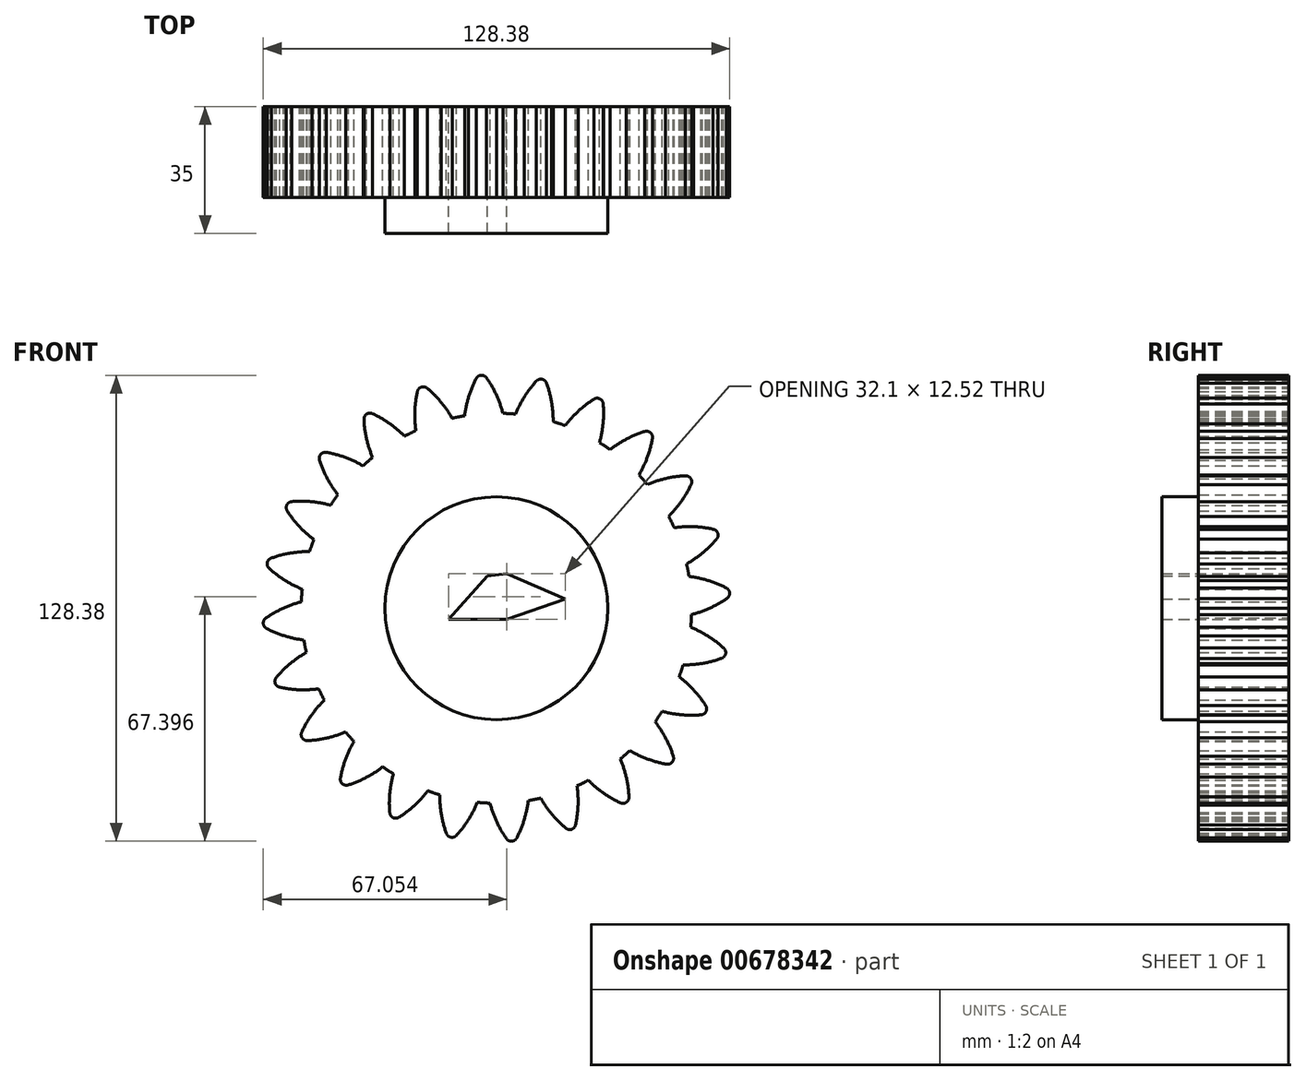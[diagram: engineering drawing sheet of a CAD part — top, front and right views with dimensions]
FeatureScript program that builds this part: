
annotation { "Feature Type Name" : "Feature", "Feature Type Description" : "" }
export const myFeature = defineFeature(function(context is Context, id is Id, definition is map)
    precondition{}
    {
        {
            var Q0;
            Q0=qCreatedBy(makeId("Front.planeOp"),FACE);
            var sketch = newSketch(context, id + "F0", { "sketchPlane" : qUnion([Q0])});
            skCircle(sketch, "E0", {"center": v(0, 0) * mm, "radius": 53.72 * mm});
            skCircle(sketch, "E1", {"center": v(0, 0) * mm, "radius": 58.67 * mm, "construction": true});
            skCircle(sketch, "E2", {"center": v(0, 0) * mm, "radius": 63.5 * mm, "construction": true});
            skLineSegment(sketch, "E3", {"start": v(0, 0) * mm, "end": v(0, 77.82) * mm, "construction": true});
            skLineSegment(sketch, "E4", {"start": v(0, 0) * mm, "end": v(-5.67, 86.58) * mm, "construction": true});
            skLineSegment(sketch, "E5", {"start": v(0, 58.67) * mm, "end": v(-52.15, 58.67) * mm, "construction": true});
            skLineSegment(sketch, "E6", {"start": v(-52.15, 58.67) * mm, "end": v(-65.26, 58.67) * mm, "construction": true});
            skLineSegment(sketch, "E7", {"start": v(0, 58.67) * mm, "end": v(-71.37, 38.87) * mm, "construction": true});
            skLineSegment(sketch, "E8", {"start": v(-55.2, 58.67) * mm, "end": v(-61.48, 58.67) * mm, "construction": true});
            skCircle(sketch, "E9", {"center": v(0, 0) * mm, "radius": 56.54 * mm, "construction": true});
            skCircle(sketch, "E10", {"center": v(0, 58.67) * mm, "radius": 30.43 * mm, "construction": true});
            skCircle(sketch, "E11", {"center": v(-27.68, 46.04) * mm, "radius": 30.43 * mm, "construction": true});
            skArc(sketch, "E12", {"start": v(0, 58.67) * mm, "mid": v(-1.24, 61.13) * mm, "end": v(-2.72, 63.44) * mm});
            skArc(sketch, "E13", {"start": v(1.77, 53.7) * mm, "mid": v(1, 56.22) * mm, "end": v(0, 58.67) * mm});
            skArc(sketch, "E14.MirrorCS", {"start": v(-7.66, 58.17) * mm, "mid": v(-6.75, 60.76) * mm, "end": v(-5.58, 63.25) * mm});
            skArc(sketch, "E15.MirrorCS", {"start": v(-8.76, 53) * mm, "mid": v(-8.33, 55.61) * mm, "end": v(-7.66, 58.17) * mm});
            skArc(sketch, "E16", {"start": v(-2.72, 63.44) * mm, "mid": v(-4.2, 64.18) * mm, "end": v(-5.58, 63.25) * mm});
            skCircle(sketch, "E17", {"center": v(0, 0) * mm, "radius": 30.7 * mm});
            skLineSegment(sketch, "E18", {"start": v(2.8, 9.47) * mm, "end": v(18.91, 2.54) * mm});
            skLineSegment(sketch, "E19", {"start": v(18.91, 2.54) * mm, "end": v(2.8, -3.06) * mm});
            skLineSegment(sketch, "E20", {"start": v(2.8, -3.06) * mm, "end": v(-13.18, -3.06) * mm});
            skLineSegment(sketch, "E21", {"start": v(-13.18, -3.06) * mm, "end": v(-2.45, 8.9) * mm});
            skLineSegment(sketch, "E22", {"start": v(-2.45, 8.9) * mm, "end": v(2.8, 9.47) * mm});
            skSolve(sketch);
        }
        {
            var Q0;
            {var subQ0=sQuery(id+"F0.wireOp",EDGE,"E0");var subQ1=makeQuery(id+"F0.imprint","INTERSECT",VERTEX,{"derivedFrom":[subQ0,sQuery(id+"F0.wireOp",EDGE,"E13")]});Q0=makeQuery(id+"F0.imprint","IMPRINT",FACE,{"disambiguationData":[TD([[makeQuery(id+"F0.imprint","IMPRINT",EDGE,{"disambiguationData":[TD([[subQ1,-1.0]])],"derivedFrom":subQ0}),1.0]])]});}
            var Q1;
            Q1=makeQuery(id+"F0.imprint","IMPRINT",FACE,{"disambiguationData":[TD([[makeQuery(id+"F0.imprint","IMPRINT",EDGE,{"derivedFrom":sQuery(id+"F0.wireOp",EDGE,"E12")}),1.0]])]});
            extrude(context, id + "F1", {"entities" : qUnion([Q0, Q1]), "depth" : 25 * mm, "offsetDistance" : 25 * mm});
        }
        {
            var Q0;
            Q0=makeQuery(id+"F1.opExtrude","SWEPT_BODY",BODY,{"disambiguationData":[OSD([sQuery(id+"F0.wireOp",EDGE,"E0"),sQuery(id+"F0.wireOp",EDGE,"E12"),sQuery(id+"F0.wireOp",EDGE,"E13"),sQuery(id+"F0.wireOp",EDGE,"E14.MirrorCS"),sQuery(id+"F0.wireOp",EDGE,"E15.MirrorCS"),sQuery(id+"F0.wireOp",EDGE,"E16")])]});
            var Q1;
            Q1=makeQuery(id+"F1.opExtrude","SWEPT_FACE",FACE,{"disambiguationData":[OSD([sQuery(id+"F0.wireOp",EDGE,"E0")])]});
            circularPattern(context, id + "F2", {"entities" : qUnion([Q0]), "axis" : qUnion([Q1]), "angle" : 360 * degree, "instanceCount" : 24, "equalSpace" : true});
        }
        {
            var Q0;
            Q0=makeQuery(id+"F0.imprint","IMPRINT",FACE,{"disambiguationData":[TD([[makeQuery(id+"F0.imprint","IMPRINT",EDGE,{"derivedFrom":sQuery(id+"F0.wireOp",EDGE,"E17")}),1.0]])]});
            extrude(context, id + "F3", {"entities" : qUnion([Q0]), "operationType" : NewBodyOperationType.ADD, "depth" : 35 * mm, "offsetDistance" : 25 * mm});
        }
    });
